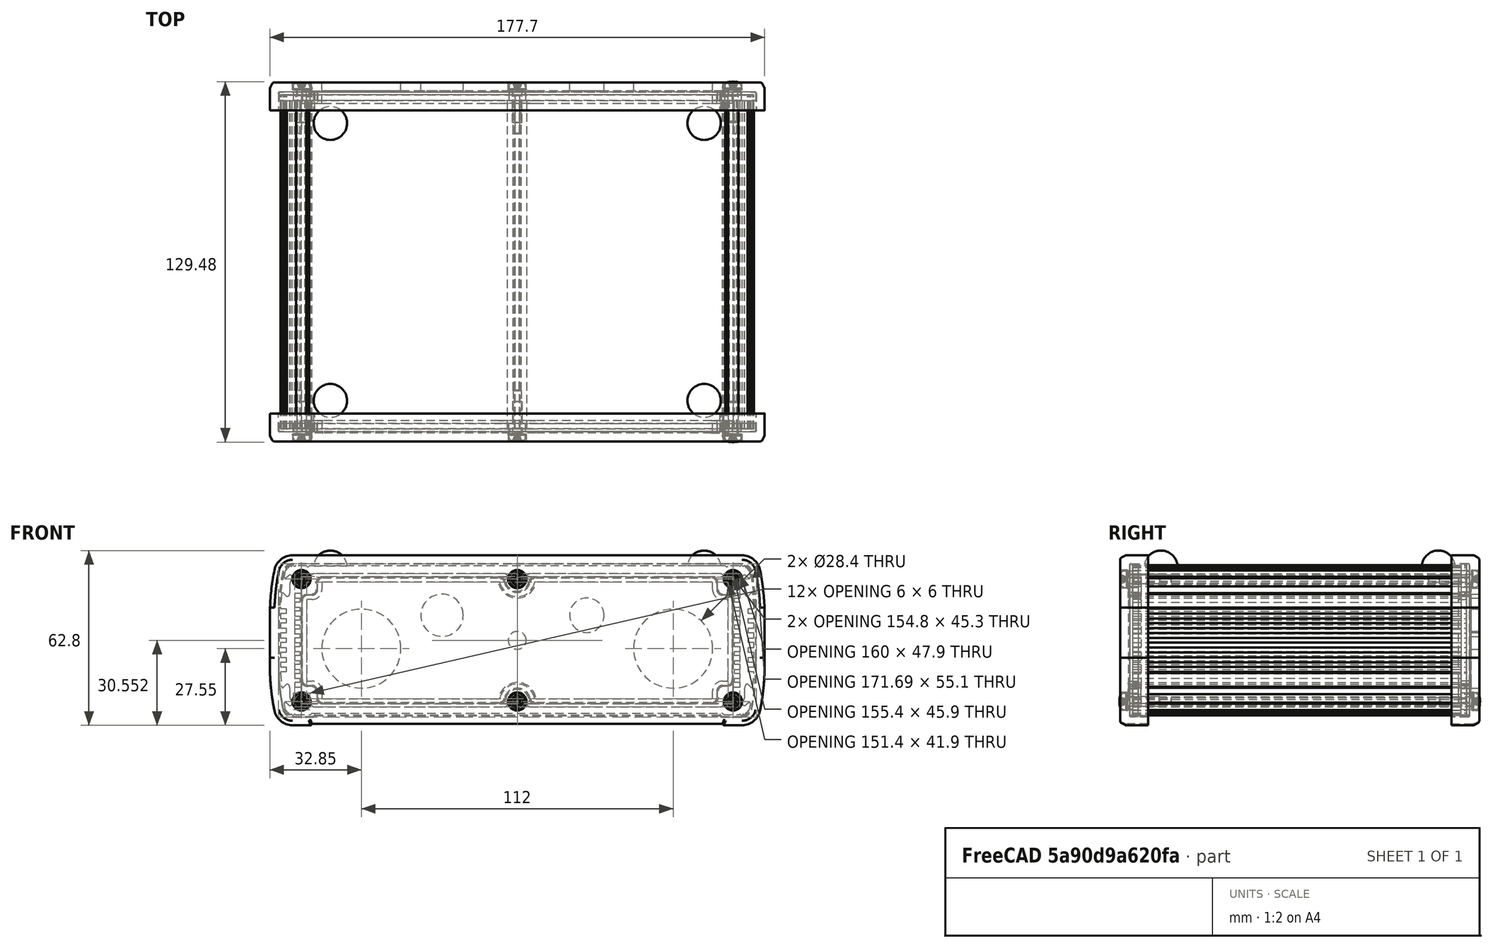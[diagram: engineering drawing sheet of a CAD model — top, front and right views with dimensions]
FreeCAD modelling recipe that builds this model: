
FCSTD DOCUMENT  (FreeCAD 0.19R24276 (Git))
Label: externalViewEX64
License: All rights reserved
LicenseURL: http://en.wikipedia.org/wiki/All_rights_reserved
objects: Part::Cylinder×5, TechDraw::DrawViewPart×3, TechDraw::DrawViewAnnotation×3, Part::Feature×1, Part::MultiFuse×1, Part::Cut×1, TechDraw::DrawSVGTemplate×1, TechDraw::DrawPage×1
note: 8 computed .brp shape members not serialized (recipe doc carries the construction recipe); baked Part::Feature solids carry a one-line shape summary decoded from their .brp

FEATURE [Part::Feature] Feature  label="EX-64-002"
  Placement = pos=(0,-43,1e-14) rot=(0,0.707107,-0.707107;3.14159rad)
  shape: bbox 178.8 x 129.6 x 63.35 mm, 1628 faces, 33 solids (baked)
FEATURE [Part::Cylinder] Cylinder  label="tSlotCut"
  Angle = 360
  AttacherType = Attacher::AttachEngine3D
  Height = 20
  Placement = pos=(0,9,0) rot=(-1,0,0;1.5708rad)
  Radius = 3.2
FEATURE [Part::Cylinder] Cylinder001  label="M3222GBH_SW0001_Cut"
  Angle = 360
  AttacherType = Attacher::AttachEngine3D
  Height = 50
  Placement = pos=(-56,-5,-3) rot=(-1,0,0;1.5708rad)
  Radius = 14.2
FEATURE [Part::Cylinder] Cylinder002  label="M3222GBH_SW0001_Cut001"
  Angle = 360
  AttacherType = Attacher::AttachEngine3D
  Height = 50
  Placement = pos=(56,-5,-3) rot=(-1,0,0;1.5708rad)
  Radius = 14.2
FEATURE [Part::Cylinder] Cylinder003  label="PG9Cut"
  Angle = 360
  AttacherType = Attacher::AttachEngine3D
  Height = 20
  Placement = pos=(-27,9,9) rot=(-1,0,0;1.5708rad)
  Radius = 7.6
FEATURE [Part::Cylinder] Cylinder004  label="PG9Cut001"
  Angle = 360
  AttacherType = Attacher::AttachEngine3D
  Height = 20
  Placement = pos=(25,9,9) rot=(-1,0,0;1.5708rad)
  Radius = 6.2
FEATURE [Part::MultiFuse] Fusion  label="cuts"
  Shapes = -> [Cylinder004,Cylinder003,Cylinder,Cylinder001,Cylinder002]
FEATURE [Part::Cut] Cut  label="Ex-64Cuts"
  Base = -> Feature
  Tool = -> Fusion
FEATURE [TechDraw::DrawSVGTemplate] Template
  EditableTexts = Designed_by_Name=Lakitha Wijeratne; Drawing_number=0.1; FC-Date=Date; FC-SC=0.60; FC-Title=UTD LoRaWAN Node; Subtitle=Version 1
  Height = 210
  Orientation = 1
  Width = 297
FEATURE [TechDraw::DrawViewPart] View  label="View 1"
  CoarseView = false
  Direction = (-0.514,0.707,-0.486)
  Focus = 100
  HardHidden = false
  IsoCount = 0
  IsoHidden = false
  IsoVisible = false
  LockPosition = false
  Perspective = false
  Rotation = 0
  Scale = 0.6
  ScaleType = 0
  SeamHidden = false
  SeamVisible = true
  SmoothHidden = false
  SmoothVisible = true
  Source = -> [Cut]
  X = 81.4283
  XDirection = (0.856,0.462,-0.233)
  Y = 158.499
FEATURE [TechDraw::DrawViewPart] View001  label="View 2"
  CoarseView = false
  Direction = (0.842,0.449,-0.299)
  Focus = 100
  HardHidden = false
  IsoCount = 0
  IsoHidden = false
  IsoVisible = false
  LockPosition = false
  Perspective = false
  Rotation = 0
  Scale = 0.6
  ScaleType = 0
  SeamHidden = false
  SeamVisible = true
  SmoothHidden = false
  SmoothVisible = true
  Source = -> [Cut]
  X = 221.05
  XDirection = (0.535,-0.626,0.568)
  Y = 128.69
FEATURE [TechDraw::DrawViewPart] View002  label="Front View"
  CoarseView = false
  Direction = (0,0,-1)
  Focus = 100
  HardHidden = false
  IsoCount = 0
  IsoHidden = false
  IsoVisible = false
  LockPosition = false
  Perspective = false
  Rotation = 0
  Scale = 0.6
  ScaleType = 0
  SeamHidden = false
  SeamVisible = true
  SmoothHidden = false
  SmoothVisible = true
  Source = -> [Cut]
  X = 71.5082
  XDirection = (1,0,0)
  Y = 62.6545
FEATURE [TechDraw::DrawViewAnnotation] Annotation  label="Annotation000"
  Font = osifont
  LineSpace = 80
  LockPosition = false
  MaxWidth = -1
  Rotation = 0
  Scale = 0.6
  ScaleType = 0
  Text = Front - Artwork
  TextSize = 5
  TextStyle = 0
  X = 84.2415
  Y = 174.293
FEATURE [TechDraw::DrawViewAnnotation] Annotation001
  Font = osifont
  LineSpace = 80
  LockPosition = false
  MaxWidth = -1
  Rotation = 0
  Scale = 0.6
  ScaleType = 0
  Text = Front - Artwork
  TextSize = 5
  TextStyle = 0
  X = 216.016
  Y = 143.2
FEATURE [TechDraw::DrawViewAnnotation] Annotation002
  Font = osifont
  LineSpace = 80
  LockPosition = false
  MaxWidth = -1
  Rotation = 0
  Scale = 0.6
  ScaleType = 0
  Text = Front - Artwork
  TextSize = 5
  TextStyle = 0
  X = 67.6586
  Y = 62.0623
FEATURE [TechDraw::DrawPage] Page
  KeepUpdated = true
  NextBalloonIndex = 1
  ProjectionType = 0
  Scale = 0.6
  Template = -> Template
  Views = -> [View,View001,View002,Annotation,Annotation001,Annotation002]
